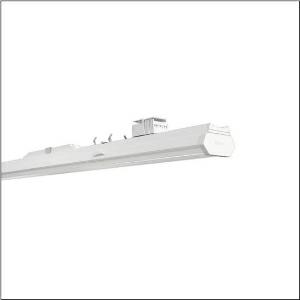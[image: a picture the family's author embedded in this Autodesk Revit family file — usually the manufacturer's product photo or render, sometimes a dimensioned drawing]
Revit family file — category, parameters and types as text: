
# Revit family: licross_r__11_protected_mo_51ts11vn465fd_08b7
name_source: partatom
category: Lighting Fixtures
units: mm (PartAtom-declared; Revit-internal decimal feet)

## family parameters
Cut with Voids When Loaded = No
Host = Face
Light Source = No
Part Type = Normal
Room Calculation Point = No
Round Connector Dimension = Use Diameter
Shared = No

## types (1)
- --- (1 x LED, 1060 lm, 8 W, 4000K)
    Apparent Load = 8 VA
    CIE Flux Codes = 83 94 98 100 100
    Color Rendering = 80
    Color Temperature = 4000K
    Default Elevation = 1800 mm
    Description = Licross® 11 Protected MO, luminaire insert, of sheet steel, galvanised, coil coated, white, length: 1.500mm, width: 90mm, height: 101mm, LED rated luminous flux: 6.910lm, light colour: 840, control gear: DALI 2, CLO, control gear: ECG DALI, with plug, 6-pole, with phase selection, mains connection: 220..240V, AC/DC, 0/50..60Hz, halogen-free wiring, for central battery installations according to DIN EN 60598-2-22, for emergency light function, without changeover relay, primary optical cover: cover, of PMMA, light emission: direct with ceiling illumination distribution, protection rating (complete): IP50, insulation class (complete): insulation class I (protective earthing), certification: CE, ENEC, VDE, UKCA, protection symbol: D if used in an environment with non-conductive dust loads with corresponding accessories, permissible ambient temperature for indoor applications: -25..+40°C, standard: EN 60598-2-22, corresponds to IFS (International Featured Standards) requirements for safety and quality in the food industry, reducing of maximum allowable ambient temperature of 5°C with ceiling mounting, packaging unit: 1 piece
    Height = 92 mm
    Lamp = 1 x LED
    Lamp Light Flux = 1060 lm
    Lamp Power = 8 W
    Lamp count = 1
    Length = 1500 mm
    Luminous efficacy = 133 lm/W
    Manufacturer = Siteco
    ModVariant = No
    Model = 51TS11VN465FD
    Mounting Place = Ceiling
    Mounting Type = Pendant
    Number of Poles = 1
    OnlyDefault = Yes
    Power Factor = 1
    Product Name = Licross® 11 Protected MO
    Product group = luminaire insert
    ProductGroupID = 902
    Protection Class = Protection class I
    Protection Degree = IP 50
    RLX_Detail_Level = 1
    RlxData = <blob elided: 24369 chars, md5=666261b1>
    Socket = socket
    Standby Power = 0 W
    System Light Flux = 1060 lm
    System Power = 8 W
    Type Comments = : DC mode (central or group accumulator) initial emergency light level
    Type Image = l_1256145.jpg
    URL = http://relux.com
    VarID = @adj_128535
    Voltage = 0 V
    Weight = 0.00 kg
    Width = 88 mm

## geometry (parser evidence)
native form markers: Blend x4, Sweep x10
no freeform markers — native parametric forms only
